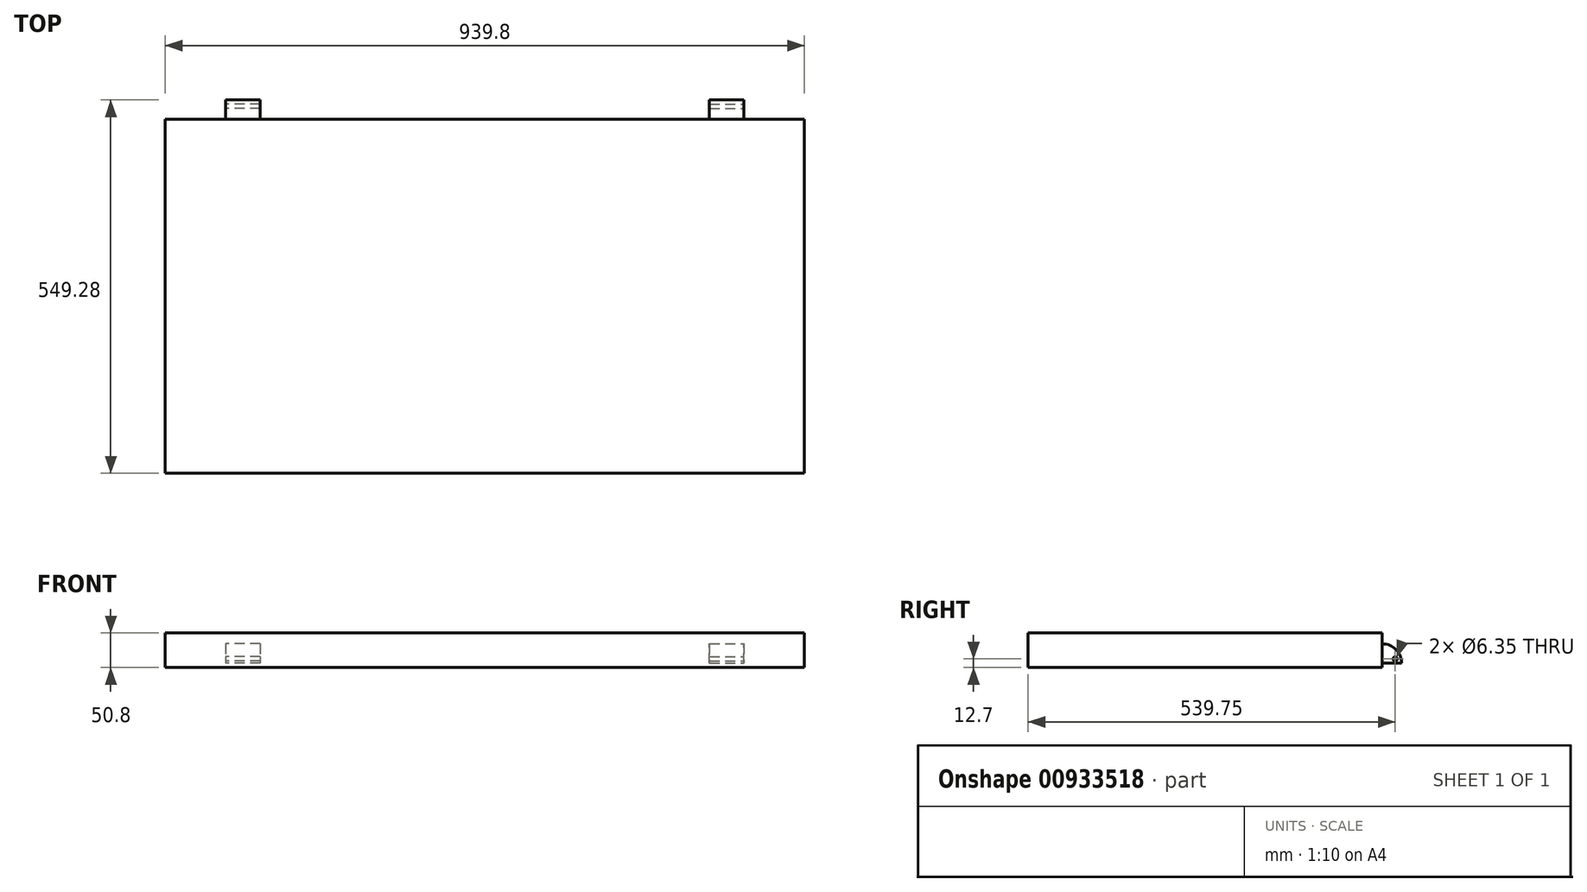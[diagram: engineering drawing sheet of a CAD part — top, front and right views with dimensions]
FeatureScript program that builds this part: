
annotation { "Feature Type Name" : "Feature", "Feature Type Description" : "" }
export const myFeature = defineFeature(function(context is Context, id is Id, definition is map)
    precondition{}
    {
        {
            var Q0;
            Q0=qCreatedBy(makeId("Top.planeOp"),FACE);
            var sketch = newSketch(context, id + "F0", { "sketchPlane" : qUnion([Q0])});
            skLineSegment(sketch, "E0.bottom", {"start": v(0, 0) * mm, "end": v(939.8, 0) * mm});
            skLineSegment(sketch, "E0.top", {"start": v(0, 520.7) * mm, "end": v(939.8, 520.7) * mm});
            skLineSegment(sketch, "E0.left", {"start": v(0, 0) * mm, "end": v(0, 520.7) * mm});
            skLineSegment(sketch, "E0.right", {"start": v(939.8, 0) * mm, "end": v(939.8, 520.7) * mm});
            skSolve(sketch);
        }
        {
            var Q0;
            Q0 = qSketchRegion(id + "F0", true);
            extrude(context, id + "F1", {"entities" : qUnion([Q0]), "depth" : 50.8 * mm, "offsetDistance" : 25.4 * mm});
        }
        {
            var Q0;
            Q0=makeQuery(id+"F1.opExtrude","SWEPT_FACE",FACE,{"disambiguationData":[OSD([sQuery(id+"F0.wireOp",EDGE,"E0.right")])]});
            cPlane(context, id + "F2", {"entities" : qUnion([Q0]), "cplaneType" : CPlaneType.OFFSET, "offset" : 88.9 * mm, "oppositeDirection" : true, "width" : 152.4 * mm, "height" : 152.4 * mm});
        }
        {
            var Q0;
            Q0=qCreatedBy(id+"F2.planeOp",FACE);
            var sketch = newSketch(context, id + "F3", { "sketchPlane" : qUnion([Q0])});
            skLineSegment(sketch, "E1", {"start": v(520.7, 34.93) * mm, "end": v(520.7, 6.35) * mm});
            skLineSegment(sketch, "E2", {"start": v(520.7, 6.35) * mm, "end": v(549.28, 6.35) * mm});
            skArc(sketch, "E3", {"start": v(549.28, 6.35) * mm, "mid": v(540.9, 26.56) * mm, "end": v(520.7, 34.92) * mm});
            skPoint(sketch, "E4", {"position": v(539.75, 12.7) * mm});
            skSolve(sketch);
        }
        {
            var Q0;
            Q0 = qSketchRegion(id + "F3", true);
            extrude(context, id + "F4", {"entities" : qUnion([Q0]), "operationType" : NewBodyOperationType.ADD, "oppositeDirection" : true, "depth" : 50.8 * mm, "offsetDistance" : 25.4 * mm});
        }
        {
            var Q0;
            Q0=sQuery(id+"F3.wireOp",VERTEX,"E4");
            var Q1;
            Q1=makeQuery(id+"F1.opExtrude","SWEPT_BODY",BODY,{"disambiguationData":[OSD([sQuery(id+"F0.wireOp",EDGE,"E0.bottom"),sQuery(id+"F0.wireOp",EDGE,"E0.top"),sQuery(id+"F0.wireOp",EDGE,"E0.left"),sQuery(id+"F0.wireOp",EDGE,"E0.right")])]});
            hole(context, id + "F5", {"style" : HoleStyle.SIMPLE, "endStyle" : HoleEndStyle.THROUGH, "holeDiameter" : 6.35 * mm, "majorDiameter" : 6.35 * mm, "isTappedThrough" : true, "tappedDepth" : 12.7 * mm, "tapClearance" : 3, "locations" : qUnion([Q0]), "scope" : qUnion([Q1])});
        }
        {
            var Q0;
            Q0=makeQuery(id+"F1.opExtrude","SWEPT_FACE",FACE,{"disambiguationData":[OSD([sQuery(id+"F0.wireOp",EDGE,"E0.left")])]});
            cPlane(context, id + "F6", {"entities" : qUnion([Q0]), "cplaneType" : CPlaneType.OFFSET, "offset" : 88.9 * mm, "oppositeDirection" : true, "width" : 152.4 * mm, "height" : 152.4 * mm});
        }
        {
            var Q0;
            Q0=qCreatedBy(id+"F6.planeOp",FACE);
            var sketch = newSketch(context, id + "F7", { "sketchPlane" : qUnion([Q0])});
            skArc(sketch, "E5.0", {"start": v(-549.28, 6.35) * mm, "mid": v(-540.9, 26.56) * mm, "end": v(-520.7, 34.92) * mm});
            skLineSegment(sketch, "E5.1", {"start": v(-520.7, 6.35) * mm, "end": v(-549.28, 6.35) * mm});
            skLineSegment(sketch, "E5.2", {"start": v(-520.7, 34.93) * mm, "end": v(-520.7, 6.35) * mm});
            skCircle(sketch, "E5.3", {"center": v(-539.75, 12.7) * mm, "radius": 3.17 * mm});
            skSolve(sketch);
        }
        {
            var Q0;
            Q0 = qSketchRegion(id + "F7", true);
            extrude(context, id + "F8", {"entities" : qUnion([Q0]), "operationType" : NewBodyOperationType.ADD, "oppositeDirection" : true, "depth" : 50.8 * mm, "offsetDistance" : 25.4 * mm});
        }
    });
